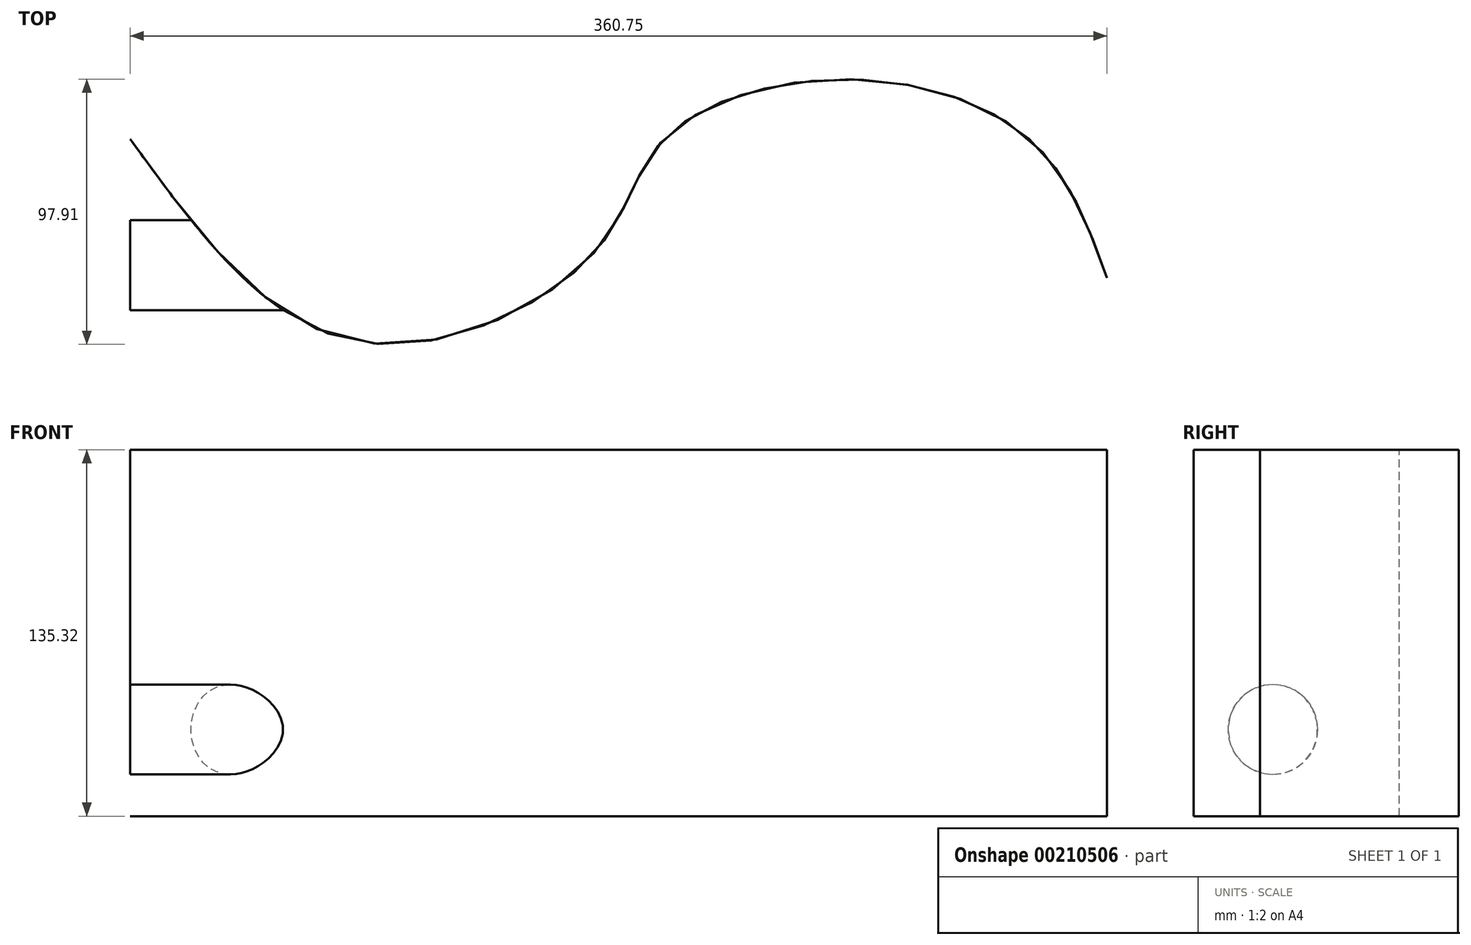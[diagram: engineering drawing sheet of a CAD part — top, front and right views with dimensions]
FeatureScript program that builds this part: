
annotation { "Feature Type Name" : "Feature", "Feature Type Description" : "" }
export const myFeature = defineFeature(function(context is Context, id is Id, definition is map)
    precondition{}
    {
        {
            var Q0;
            Q0=qCreatedBy(makeId("Top.planeOp"),FACE);
            var sketch = newSketch(context, id + "F0", { "sketchPlane" : qUnion([Q0])});
            skFitSpline(sketch, "E0", {"points": [v(0, 0) * mm, v(83.85, -74.85) * mm, v(171.28, -42.21) * mm, v(197.23, 0) * mm, v(261.7, 22.03) * mm, v(332.06, 0) * mm, v(360.75, -51.4) * mm], "startDerivative": vector(365.07, -504.3) * mm, "endDerivative": vector(139.18, -386.16) * mm});
            skSolve(sketch);
        }
        {
            var Q0;
            Q0=sQuery(id+"F0.wireOp",EDGE,"E0");
            extrude(context, id + "F1", {"bodyType" : ToolBodyType.SURFACE, "surfaceEntities" : qUnion([Q0]), "depth" : 135.33 * mm, "symmetric" : true});
        }
        {
            var Q0;
            Q0=qCreatedBy(makeId("Right.planeOp"),FACE);
            var sketch = newSketch(context, id + "F2", { "sketchPlane" : qUnion([Q0])});
            skCircle(sketch, "E1", {"center": v(-46.64, -35.64) * mm, "radius": 16.6 * mm});
            skSolve(sketch);
        }
        {
            var Q0;
            Q0=makeQuery(id+"F2.imprint","IMPRINT",FACE,{"disambiguationData":[TD([[makeQuery(id+"F2.imprint","IMPRINT",EDGE,{"derivedFrom":sQuery(id+"F2.wireOp",EDGE,"E1")}),1.0]])]});
            var Q1;
            Q1=sQuery(id+"F2.wireOp",EDGE,"E1");
            extrude(context, id + "F3", {"entities" : qUnion([Q0]), "bodyType" : ToolBodyType.SURFACE, "operationType" : NewBodyOperationType.ADD, "surfaceEntities" : qUnion([Q1]), "endBound" : BoundingType.UP_TO_NEXT, "depth" : 25 * mm});
        }
    });
